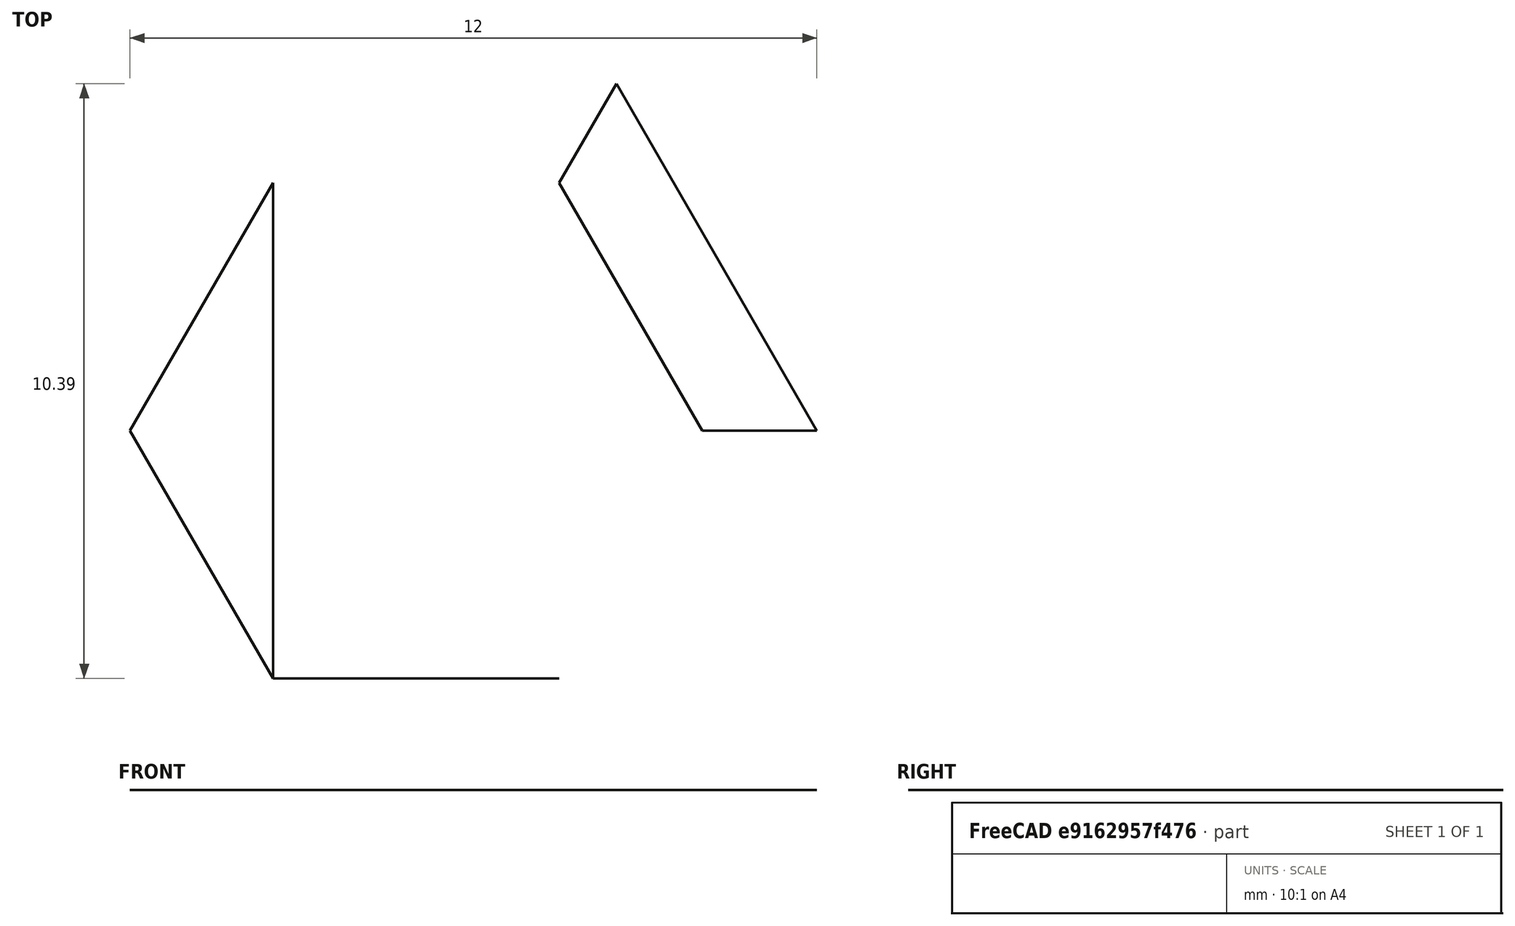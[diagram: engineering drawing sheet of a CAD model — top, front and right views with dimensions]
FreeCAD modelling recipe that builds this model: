
FCSTD DOCUMENT  (FreeCAD 0.21R33771 (Git))
Label: Primitives
License: All rights reserved
LicenseURL: https://en.wikipedia.org/wiki/All_rights_reserved
objects: Part::Feature×6, Part::RegularPolygon×2, Part::Circle×1
note: 9 computed .brp shape members not serialized (recipe doc carries the construction recipe); baked Part::Feature solids carry a one-line shape summary decoded from their .brp

FEATURE [Part::RegularPolygon] RegularPolygon  label="Regular polygon"
  AttacherType = Attacher::AttachEngine3D
  Circumradius = 5
  Polygon = 6
FEATURE [Part::RegularPolygon] RegularPolygon001  label="Regular polygon001"
  AttacherType = Attacher::AttachEngine3D
  Circumradius = 7
  Polygon = 6
FEATURE [Part::Circle] Circle
  Angle1 = 0
  Angle2 = 360
  AttacherType = Attacher::AttachEngine3D
  Radius = 9
FEATURE [Part::Feature] Edge
  shape: bbox 1 x 1.732 x 2e-07 mm, 0 faces, 0 solids (baked)
FEATURE [Part::Feature] Edge001
  shape: bbox 2 x 2e-07 x 2e-07 mm, 0 faces, 0 solids (baked)
FEATURE [Part::Feature] Wire
  Placement = pos=(0,-1,0) rot=(0,0,1;0rad)
  shape: bbox 7 x 2e-07 x 2e-07 mm, 0 faces, 0 solids (baked)
FEATURE [Part::Feature] Face
  shape: bbox 2.75 x 9.526 x 2e-07 mm, 1 faces, 0 solids (baked)
FEATURE [Part::Feature] Face001
  shape: bbox 5.5 x 0.0011 x 2e-07 mm, 1 faces, 0 solids (baked)
FEATURE [Part::Feature] Face002
  shape: bbox 5.5 x 7.621 x 2e-07 mm, 1 faces, 0 solids (baked)
